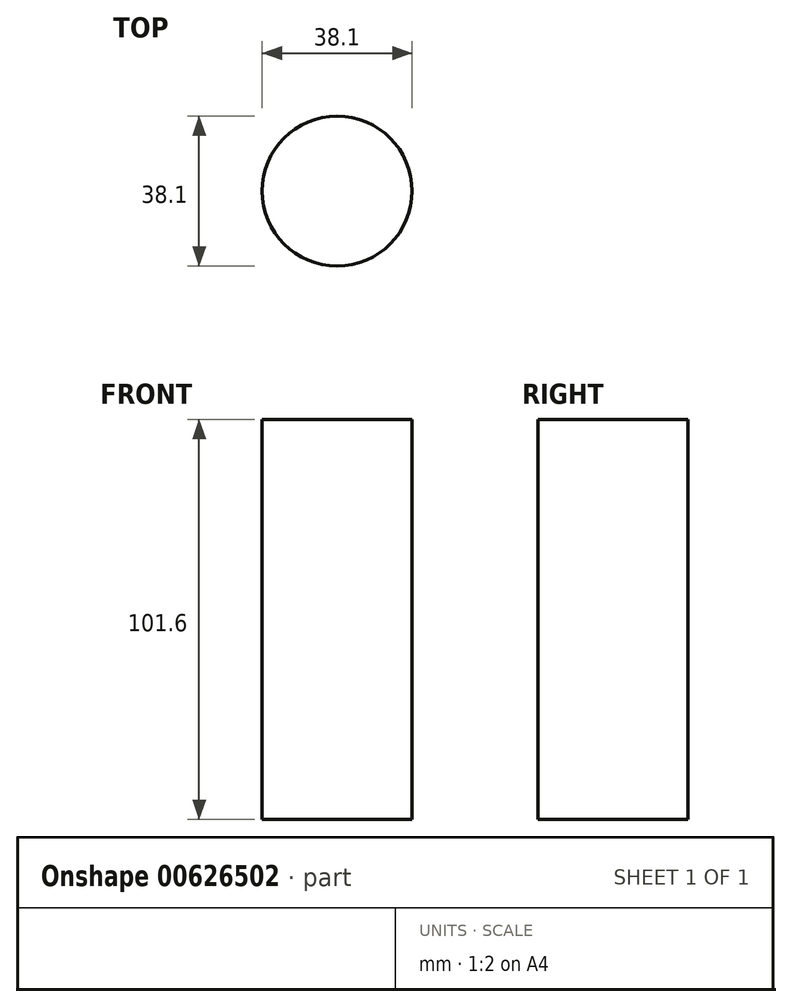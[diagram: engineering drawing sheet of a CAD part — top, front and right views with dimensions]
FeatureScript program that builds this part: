
annotation { "Feature Type Name" : "Feature", "Feature Type Description" : "" }
export const myFeature = defineFeature(function(context is Context, id is Id, definition is map)
    precondition{}
    {
        {
            var Q0;
            Q0=qCreatedBy(makeId("Top.planeOp"),FACE);
            var sketch = newSketch(context, id + "F0", { "sketchPlane" : qUnion([Q0])});
            skCircle(sketch, "E0", {"center": v(0, 0) * mm, "radius": 19.05 * mm});
            skSolve(sketch);
        }
        {
            var Q0;
            Q0 = qSketchRegion(id + "F0", true);
            extrude(context, id + "F1", {"entities" : qUnion([Q0]), "depth" : 101.6 * mm, "offsetDistance" : 25.4 * mm});
        }
    });
